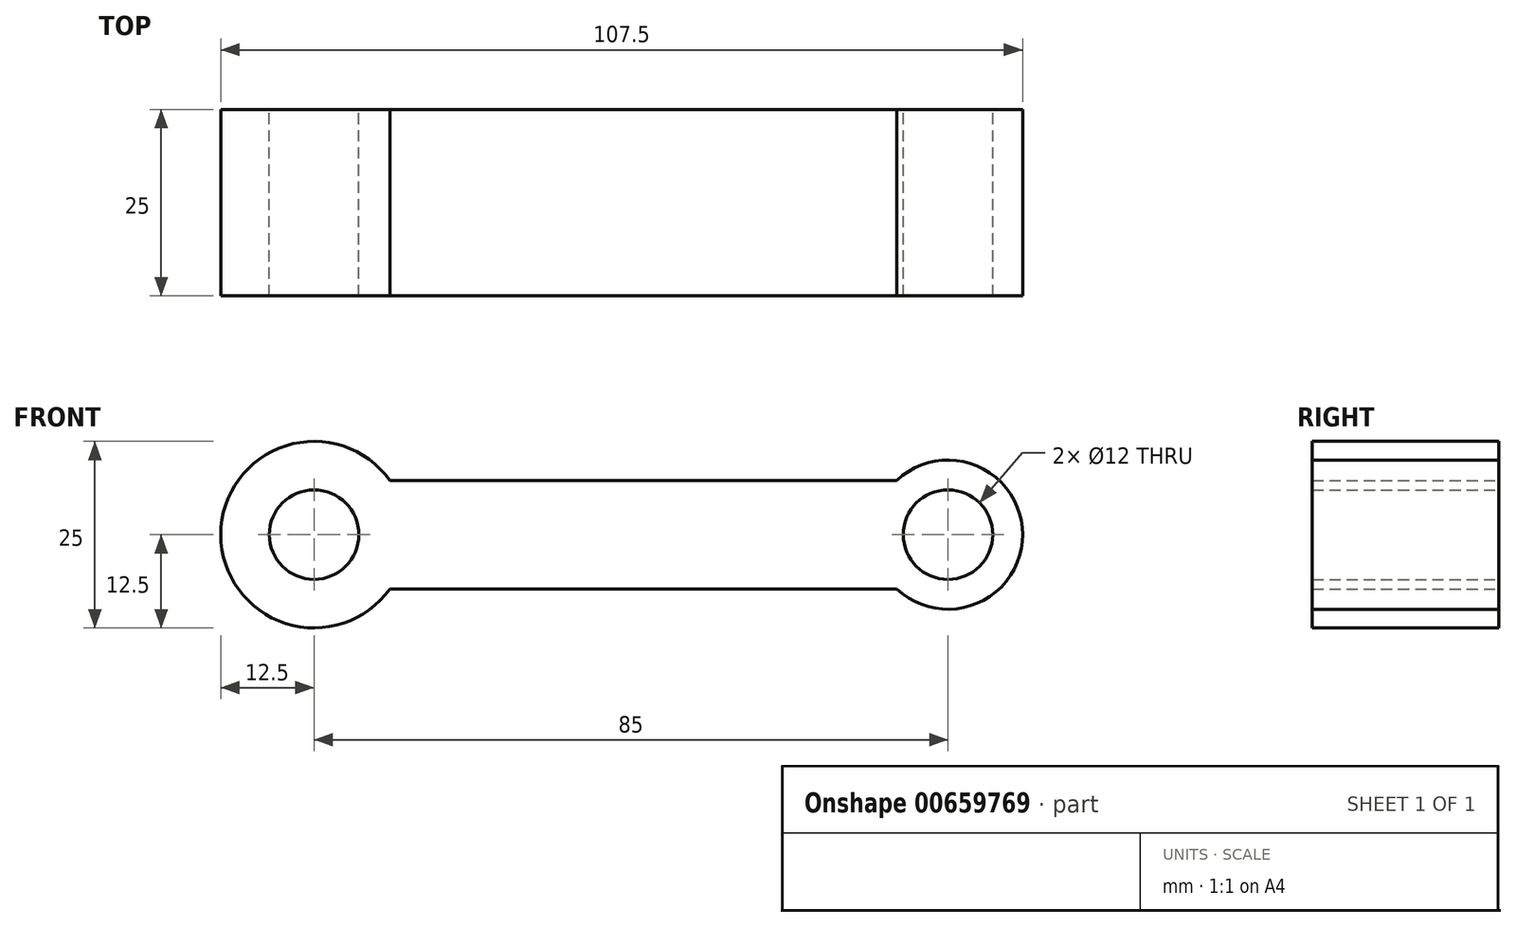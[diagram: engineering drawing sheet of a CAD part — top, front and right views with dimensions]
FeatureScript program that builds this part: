
annotation { "Feature Type Name" : "Feature", "Feature Type Description" : "" }
export const myFeature = defineFeature(function(context is Context, id is Id, definition is map)
    precondition{}
    {
        {
            var Q0;
            Q0=qCreatedBy(makeId("Front.planeOp"), FACE);
            var sketch = newSketch(context, id + "F0", { "sketchPlane" : qUnion([Q0])});
            skCircle(sketch, "E0", {"center": v(0, 0) * mm, "radius": 12.5 * mm});
            skCircle(sketch, "E1", {"center": v(85, 0) * mm, "radius": 10 * mm});
            skLineSegment(sketch, "E2", {"start": v(0, 0) * mm, "end": v(85, 0) * mm, "construction": true});
            skCircle(sketch, "E3", {"center": v(0, 0) * mm, "radius": 6 * mm});
            skCircle(sketch, "E4", {"center": v(85, 0) * mm, "radius": 6 * mm});
            skLineSegment(sketch, "E5", {"start": v(10.17, 7.26) * mm, "end": v(78.12, 7.26) * mm});
            skLineSegment(sketch, "E6.MirrorCS", {"start": v(10.17, -7.26) * mm, "end": v(78.12, -7.26) * mm});
            skSolve(sketch);
        }
        {
            var Q0;
            Q0 = qSketchRegion(id + "F0", true);
            extrude(context, id + "F1", {"entities" : qUnion([Q0]), "depth" : 25 * mm, "offsetDistance" : 25 * mm});
        }
    });
